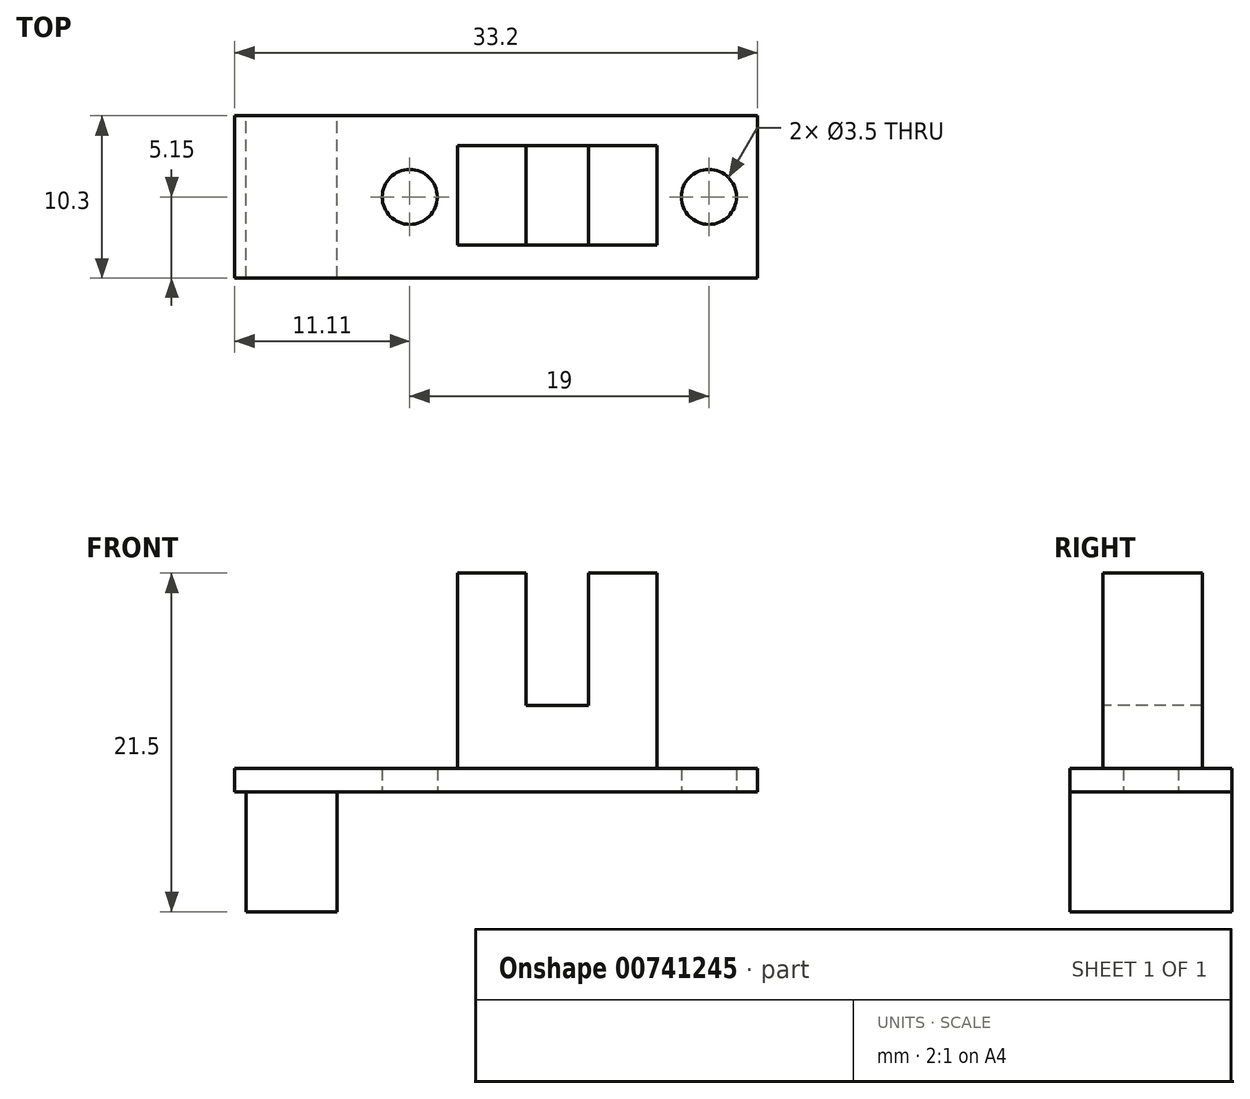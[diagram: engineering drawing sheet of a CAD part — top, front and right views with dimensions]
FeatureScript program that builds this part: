
annotation { "Feature Type Name" : "Feature", "Feature Type Description" : "" }
export const myFeature = defineFeature(function(context is Context, id is Id, definition is map)
    precondition{}
    {
        {
            var Q0;
            Q0=qCreatedBy(makeId("Top.planeOp"),FACE);
            var sketch = newSketch(context, id + "F0", { "sketchPlane" : qUnion([Q0])});
            skLineSegment(sketch, "E0.bottom", {"start": v(0, 0) * mm, "end": v(33.2, 0) * mm});
            skLineSegment(sketch, "E0.top", {"start": v(0, -10.3) * mm, "end": v(33.2, -10.3) * mm});
            skLineSegment(sketch, "E0.left", {"start": v(0, 0) * mm, "end": v(0, -10.3) * mm});
            skLineSegment(sketch, "E0.right", {"start": v(33.2, 0) * mm, "end": v(33.2, -10.3) * mm});
            skCircle(sketch, "E1", {"center": v(30.11, -5.15) * mm, "radius": 1.75 * mm});
            skCircle(sketch, "E2", {"center": v(11.11, -5.15) * mm, "radius": 1.75 * mm});
            skSolve(sketch);
        }
        {
            var Q0;
            Q0=qSketchRegion(id+"F0",true);
            extrude(context, id + "F1", {"entities" : qUnion([Q0]), "depth" : 1.5 * mm});
        }
        {
            var Q0;
            Q0=makeQuery(id+"F1.opExtrude","CAP_FACE",FACE,{"disambiguationData":[OSD([sQuery(id+"F0.wireOp",EDGE,"E0.bottom"),sQuery(id+"F0.wireOp",EDGE,"E0.top"),sQuery(id+"F0.wireOp",EDGE,"E0.left"),sQuery(id+"F0.wireOp",EDGE,"E0.right"),sQuery(id+"F0.wireOp",EDGE,"E1"),sQuery(id+"F0.wireOp",EDGE,"E2")])],"isStart":false});
            var sketch = newSketch(context, id + "F2", { "sketchPlane" : qUnion([Q0])});
            skLineSegment(sketch, "E3.0", {"start": v(33.2, 0) * mm, "end": v(33.2, -10.3) * mm, "construction": true});
            skLineSegment(sketch, "E4.0", {"start": v(0, -10.3) * mm, "end": v(33.2, -10.3) * mm, "construction": true});
            skLineSegment(sketch, "E5.bottom", {"start": v(14.16, -1.9) * mm, "end": v(26.8, -1.9) * mm});
            skLineSegment(sketch, "E5.top", {"start": v(14.16, -8.2) * mm, "end": v(26.8, -8.2) * mm});
            skLineSegment(sketch, "E5.left", {"start": v(14.16, -1.9) * mm, "end": v(14.16, -8.2) * mm});
            skLineSegment(sketch, "E5.right", {"start": v(26.8, -1.9) * mm, "end": v(26.8, -8.2) * mm});
            skSolve(sketch);
        }
        {
            var Q0;
            Q0=qSketchRegion(id+"F2",true);
            extrude(context, id + "F3", {"entities" : qUnion([Q0]), "depth" : 4 * mm});
        }
        {
            var Q0;
            Q0=makeQuery(id+"F3.opExtrude","CAP_FACE",FACE,{"disambiguationData":[OSD([sQuery(id+"F2.wireOp",EDGE,"E5.bottom"),sQuery(id+"F2.wireOp",EDGE,"E5.top"),sQuery(id+"F2.wireOp",EDGE,"E5.left"),sQuery(id+"F2.wireOp",EDGE,"E5.right")])],"isStart":false});
            var sketch = newSketch(context, id + "F4", { "sketchPlane" : qUnion([Q0])});
            skLineSegment(sketch, "E6.bottom", {"start": v(14.16, -1.9) * mm, "end": v(18.49, -1.9) * mm});
            skLineSegment(sketch, "E6.top", {"start": v(14.16, -8.2) * mm, "end": v(18.49, -8.2) * mm});
            skLineSegment(sketch, "E6.left", {"start": v(14.16, -1.9) * mm, "end": v(14.16, -8.2) * mm});
            skLineSegment(sketch, "E6.right", {"start": v(18.49, -1.9) * mm, "end": v(18.49, -8.2) * mm});
            skLineSegment(sketch, "E7.bottom", {"start": v(26.8, -1.9) * mm, "end": v(22.47, -1.9) * mm});
            skLineSegment(sketch, "E7.top", {"start": v(26.8, -8.2) * mm, "end": v(22.47, -8.2) * mm});
            skLineSegment(sketch, "E7.left", {"start": v(26.8, -1.9) * mm, "end": v(26.8, -8.2) * mm});
            skLineSegment(sketch, "E7.right", {"start": v(22.47, -1.9) * mm, "end": v(22.47, -8.2) * mm});
            skSolve(sketch);
        }
        {
            var Q0;
            Q0=qSketchRegion(id+"F4",true);
            extrude(context, id + "F5", {"entities" : qUnion([Q0]), "operationType" : NewBodyOperationType.ADD, "depth" : 8.4 * mm});
        }
        {
            var Q0;
            Q0=makeQuery(id+"F1.opExtrude","CAP_FACE",FACE,{"disambiguationData":[OSD([sQuery(id+"F0.wireOp",EDGE,"E0.bottom"),sQuery(id+"F0.wireOp",EDGE,"E0.top"),sQuery(id+"F0.wireOp",EDGE,"E0.left"),sQuery(id+"F0.wireOp",EDGE,"E0.right"),sQuery(id+"F0.wireOp",EDGE,"E1"),sQuery(id+"F0.wireOp",EDGE,"E2")])],"isStart":true});
            var sketch = newSketch(context, id + "F6", { "sketchPlane" : qUnion([Q0])});
            skLineSegment(sketch, "E8.bottom", {"start": v(6.48, 10.3) * mm, "end": v(0.7, 10.3) * mm});
            skLineSegment(sketch, "E8.top", {"start": v(6.48, 0) * mm, "end": v(0.7, 0) * mm});
            skLineSegment(sketch, "E8.left", {"start": v(6.48, 10.3) * mm, "end": v(6.48, 0) * mm});
            skLineSegment(sketch, "E8.right", {"start": v(0.7, 10.3) * mm, "end": v(0.7, 0) * mm});
            skSolve(sketch);
        }
        {
            var Q0;
            Q0=qSketchRegion(id+"F6",true);
            extrude(context, id + "F7", {"entities" : qUnion([Q0]), "depth" : 7.6 * mm});
        }
    });
